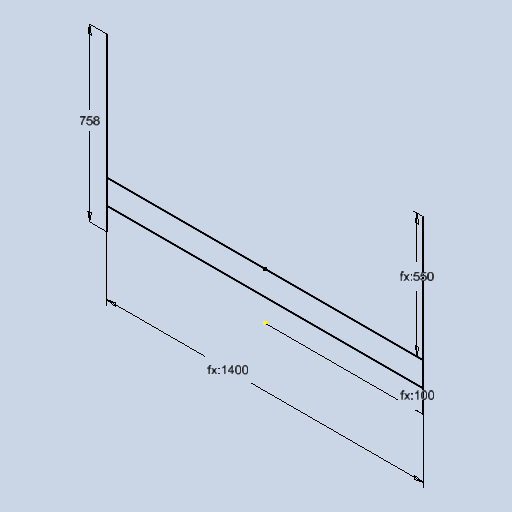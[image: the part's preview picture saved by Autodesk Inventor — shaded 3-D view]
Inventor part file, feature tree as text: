
AUTODESK INVENTOR PART (.ipt)
format: ipt  version: 2025 (Build 290162010, 162A)  size: 261,632 bytes
history: native  units: mm
features: sketch x1
ambient origin geometry x8: Origin, YZ Plane, XZ Plane, XY Plane, X Axis, Y Axis, Z Axis, Center Point
feature tree (1):
  sketch  "Sketch1"  dims[d0=758.0mm d1=1400.0mm d2=100.0mm d4=550.0mm]
